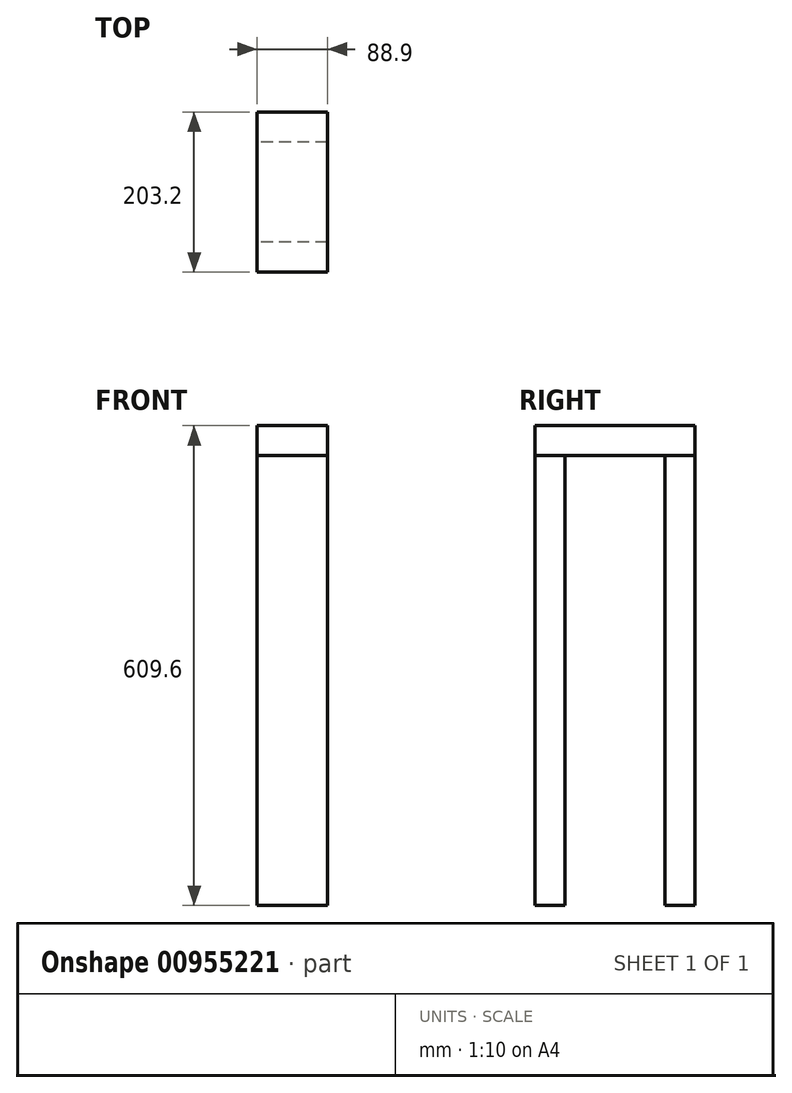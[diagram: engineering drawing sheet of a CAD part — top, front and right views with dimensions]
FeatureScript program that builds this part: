
annotation { "Feature Type Name" : "Feature", "Feature Type Description" : "" }
export const myFeature = defineFeature(function(context is Context, id is Id, definition is map)
    precondition{}
    {
        {
            var Q0;
            Q0=qCreatedBy(makeId("Front.planeOp"),FACE);
            var sketch = newSketch(context, id + "F0", { "sketchPlane" : qUnion([Q0])});
            skLineSegment(sketch, "E0.bottom", {"start": v(-44.45, 609.6) * mm, "end": v(44.45, 609.6) * mm});
            skLineSegment(sketch, "E0.top", {"start": v(-44.45, 571.5) * mm, "end": v(44.45, 571.5) * mm});
            skLineSegment(sketch, "E0.left", {"start": v(-44.45, 609.6) * mm, "end": v(-44.45, 571.5) * mm});
            skLineSegment(sketch, "E0.right", {"start": v(44.45, 609.6) * mm, "end": v(44.45, 571.5) * mm});
            skPoint(sketch, "E1", {"position": v(0, 571.5) * mm});
            skSolve(sketch);
        }
        {
            var Q0;
            Q0=makeQuery(id+"F0.imprint","IMPRINT",FACE,{"disambiguationData":[TD([[makeQuery(id+"F0.imprint","IMPRINT",EDGE,{"derivedFrom":sQuery(id+"F0.wireOp",EDGE,"E0.bottom")}),-1.0]])]});
            extrude(context, id + "F1", {"entities" : qUnion([Q0]), "endBound" : BoundingType.SYMMETRIC, "depth" : 203.2 * mm, "offsetDistance" : 25.4 * mm});
        }
        {
            var Q0;
            Q0=makeQuery(id+"F1.opExtrude","SWEPT_FACE",FACE,{"disambiguationData":[OSD([sQuery(id+"F0.wireOp",EDGE,"E0.top")])]});
            var sketch = newSketch(context, id + "F2", { "sketchPlane" : qUnion([Q0])});
            skLineSegment(sketch, "E2.bottom", {"start": v(-44.45, -101.6) * mm, "end": v(44.45, -101.6) * mm});
            skLineSegment(sketch, "E2.top", {"start": v(-44.45, -63.5) * mm, "end": v(44.45, -63.5) * mm});
            skLineSegment(sketch, "E2.left", {"start": v(-44.45, -101.6) * mm, "end": v(-44.45, -63.5) * mm});
            skLineSegment(sketch, "E2.right", {"start": v(44.45, -101.6) * mm, "end": v(44.45, -63.5) * mm});
            skLineSegment(sketch, "E3.bottom", {"start": v(-44.45, 101.6) * mm, "end": v(44.45, 101.6) * mm});
            skLineSegment(sketch, "E3.top", {"start": v(-44.45, 63.5) * mm, "end": v(44.45, 63.5) * mm});
            skLineSegment(sketch, "E3.left", {"start": v(-44.45, 101.6) * mm, "end": v(-44.45, 63.5) * mm});
            skLineSegment(sketch, "E3.right", {"start": v(44.45, 101.6) * mm, "end": v(44.45, 63.5) * mm});
            skSolve(sketch);
        }
        {
            var Q0;
            Q0=makeQuery(id+"F2.imprint","IMPRINT",FACE,{"disambiguationData":[TD([[makeQuery(id+"F2.imprint","IMPRINT",EDGE,{"derivedFrom":sQuery(id+"F2.wireOp",EDGE,"E2.bottom")}),1.0]])]});
            var Q1;
            Q1=makeQuery(id+"F2.imprint","IMPRINT",FACE,{"disambiguationData":[TD([[makeQuery(id+"F2.imprint","IMPRINT",EDGE,{"derivedFrom":sQuery(id+"F2.wireOp",EDGE,"E3.bottom")}),-1.0]])]});
            var Q2;
            Q2=qCreatedBy(makeId("Top.planeOp"),FACE);
            extrude(context, id + "F3", {"entities" : qUnion([Q0, Q1]), "endBound" : BoundingType.UP_TO_SURFACE, "depth" : 25.4 * mm, "endBoundEntityFace" : qUnion([Q2]), "offsetDistance" : 25.4 * mm});
        }
    });
